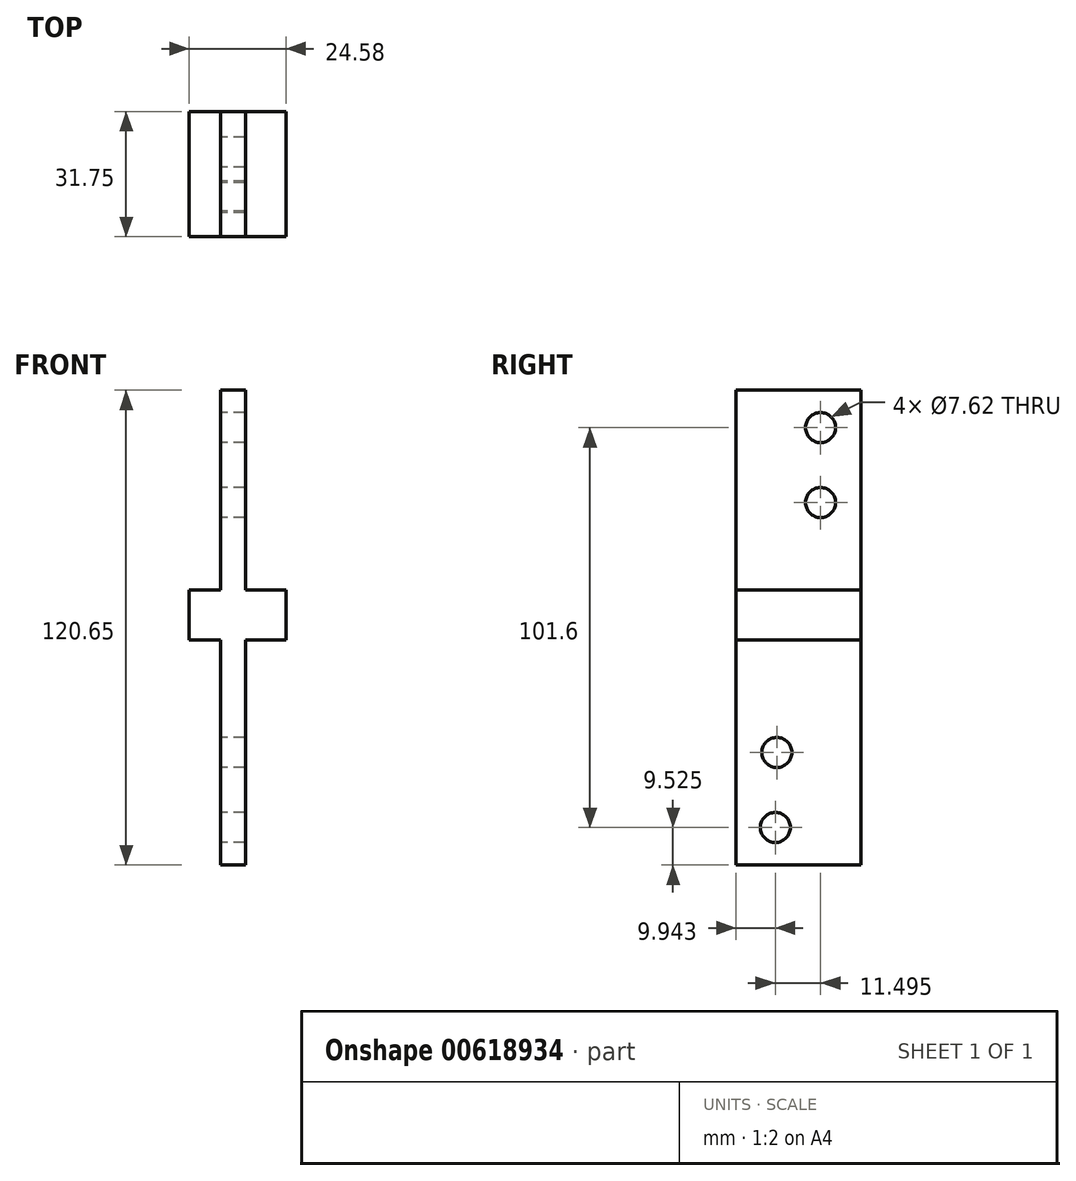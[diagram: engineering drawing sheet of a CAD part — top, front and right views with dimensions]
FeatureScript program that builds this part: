
annotation { "Feature Type Name" : "Feature", "Feature Type Description" : "" }
export const myFeature = defineFeature(function(context is Context, id is Id, definition is map)
    precondition{}
    {
        {
            var Q0;
            Q0=qCreatedBy(makeId("Front.planeOp"),FACE);
            var sketch = newSketch(context, id + "F0", { "sketchPlane" : qUnion([Q0])});
            skLineSegment(sketch, "E0", {"start": v(0, 0) * mm, "end": v(0, 50.8) * mm});
            skLineSegment(sketch, "E1", {"start": v(0, 50.8) * mm, "end": v(6.35, 50.8) * mm});
            skLineSegment(sketch, "E2", {"start": v(6.35, 50.8) * mm, "end": v(6.35, 0) * mm});
            skLineSegment(sketch, "E3", {"start": v(6.35, 0) * mm, "end": v(16.66, 0) * mm});
            skLineSegment(sketch, "E4", {"start": v(16.66, 0) * mm, "end": v(16.66, -12.7) * mm});
            skLineSegment(sketch, "E5", {"start": v(16.66, -12.7) * mm, "end": v(6.35, -12.7) * mm});
            skLineSegment(sketch, "E6", {"start": v(6.35, -12.7) * mm, "end": v(6.35, -69.85) * mm});
            skLineSegment(sketch, "E7", {"start": v(6.35, -69.85) * mm, "end": v(0, -69.85) * mm});
            skLineSegment(sketch, "E8", {"start": v(0, -69.85) * mm, "end": v(0, -12.7) * mm});
            skLineSegment(sketch, "E9", {"start": v(0, -12.7) * mm, "end": v(-7.92, -12.7) * mm});
            skLineSegment(sketch, "E10", {"start": v(-7.92, -12.7) * mm, "end": v(-7.92, 0) * mm});
            skLineSegment(sketch, "E11", {"start": v(-7.92, 0) * mm, "end": v(0, 0) * mm});
            skSolve(sketch);
        }
        {
            var Q0;
            Q0=qSketchRegion(id+"F0",true);
            extrude(context, id + "F1", {"entities" : qUnion([Q0]), "depth" : 31.75 * mm, "offsetDistance" : 25.4 * mm});
        }
        {
            var Q0;
            Q0=makeQuery(id+"F1.opExtrude","SWEPT_FACE",FACE,{"disambiguationData":[OSD([sQuery(id+"F0.wireOp",EDGE,"E0")])]});
            var sketch = newSketch(context, id + "F2", { "sketchPlane" : qUnion([Q0])});
            skCircle(sketch, "E12", {"center": v(10.31, 41.27) * mm, "radius": 3.81 * mm});
            skSolve(sketch);
        }
        {
            var Q0;
            Q0=makeQuery(id+"F1.opExtrude","SWEPT_FACE",FACE,{"disambiguationData":[OSD([sQuery(id+"F0.wireOp",EDGE,"E0")])]});
            var sketch = newSketch(context, id + "F3", { "sketchPlane" : qUnion([Q0])});
            skCircle(sketch, "E13", {"center": v(10.31, 22.23) * mm, "radius": 3.81 * mm});
            skSolve(sketch);
        }
        {
            var Q0;
            Q0=makeQuery(id+"F1.opExtrude","SWEPT_FACE",FACE,{"disambiguationData":[OSD([sQuery(id+"F0.wireOp",EDGE,"E8")])]});
            var sketch = newSketch(context, id + "F4", { "sketchPlane" : qUnion([Q0])});
            skCircle(sketch, "E14", {"center": v(21.44, -41.28) * mm, "radius": 3.8 * mm});
            skCircle(sketch, "E15", {"center": v(21.8, -60.33) * mm, "radius": 3.81 * mm});
            skSolve(sketch);
        }
        {
            var Q0;
            Q0=sQuery(id+"F2.wireOp",VERTEX,"E12.center");
            var Q1;
            Q1=sQuery(id+"F3.wireOp",VERTEX,"E13.center");
            var Q2;
            Q2=sQuery(id+"F4.wireOp",VERTEX,"E14.center");
            var Q3;
            Q3=sQuery(id+"F4.wireOp",VERTEX,"E15.center");
            var Q4;
            Q4=makeQuery(id+"F1.opExtrude","SWEPT_BODY",BODY,{"disambiguationData":[OSD([sQuery(id+"F0.wireOp",EDGE,"E0"),sQuery(id+"F0.wireOp",EDGE,"E1"),sQuery(id+"F0.wireOp",EDGE,"E2"),sQuery(id+"F0.wireOp",EDGE,"E3"),sQuery(id+"F0.wireOp",EDGE,"E4"),sQuery(id+"F0.wireOp",EDGE,"E5"),sQuery(id+"F0.wireOp",EDGE,"E6"),sQuery(id+"F0.wireOp",EDGE,"E7"),sQuery(id+"F0.wireOp",EDGE,"E8"),sQuery(id+"F0.wireOp",EDGE,"E9"),sQuery(id+"F0.wireOp",EDGE,"E10"),sQuery(id+"F0.wireOp",EDGE,"E11")])]});
            hole(context, id + "F5", {"style" : HoleStyle.SIMPLE, "endStyle" : HoleEndStyle.THROUGH, "holeDiameter" : 7.62 * mm, "majorDiameter" : 6.35 * mm, "isTappedThrough" : true, "tappedDepth" : 12.7 * mm, "tapClearance" : 3, "locations" : qUnion([Q0, Q1, Q2, Q3]), "scope" : qUnion([Q4])});
        }
    });
